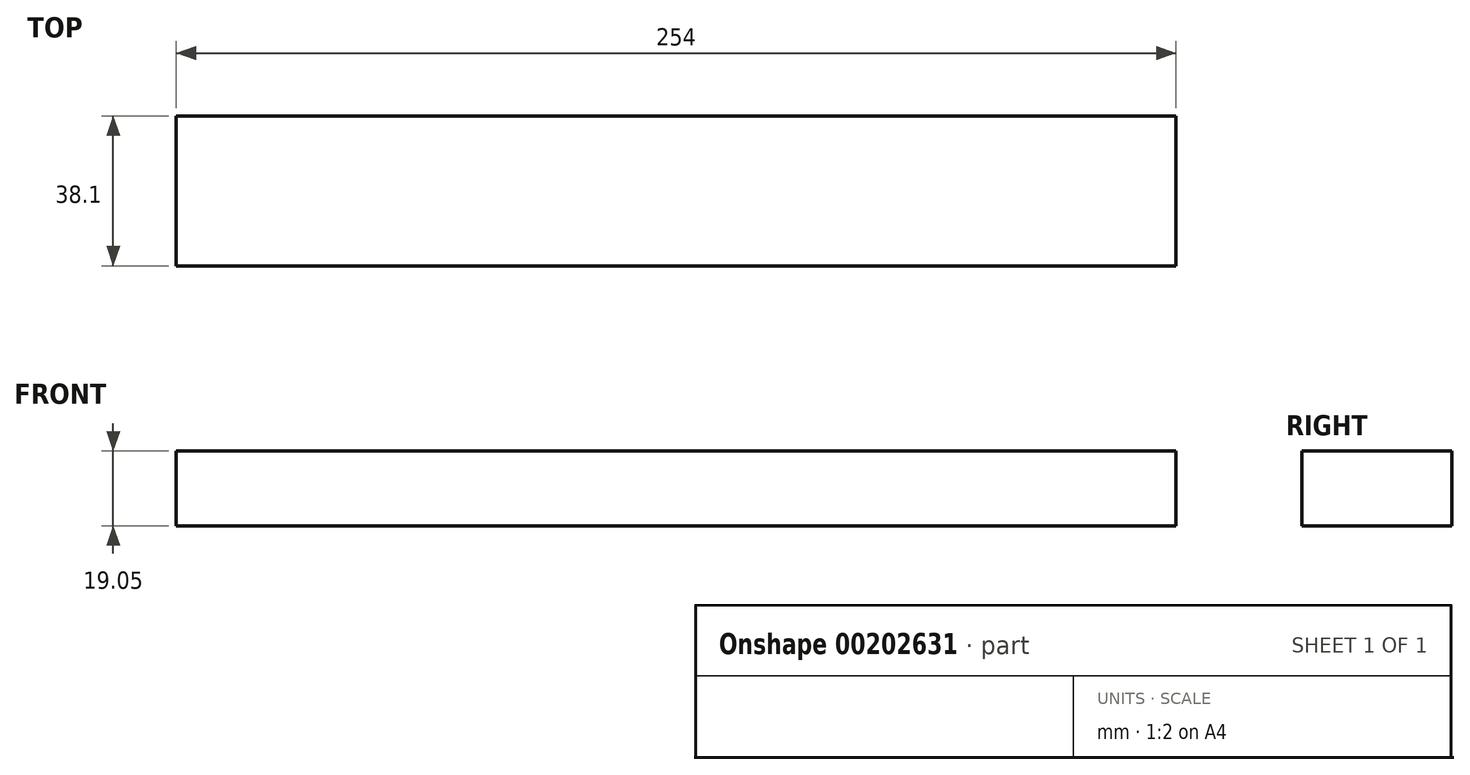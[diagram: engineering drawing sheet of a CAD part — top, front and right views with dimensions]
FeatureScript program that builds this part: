
annotation { "Feature Type Name" : "Feature", "Feature Type Description" : "" }
export const myFeature = defineFeature(function(context is Context, id is Id, definition is map)
    precondition{}
    {
        {
            var Q0;
            Q0=qCreatedBy(makeId("Top.planeOp"),FACE);
            var sketch = newSketch(context, id + "F0", { "sketchPlane" : qUnion([Q0])});
            skLineSegment(sketch, "E0.bottom", {"start": v(0, 0) * mm, "end": v(254, 0) * mm});
            skLineSegment(sketch, "E0.top", {"start": v(0, 38.1) * mm, "end": v(254, 38.1) * mm});
            skLineSegment(sketch, "E0.left", {"start": v(0, 0) * mm, "end": v(0, 38.1) * mm});
            skLineSegment(sketch, "E0.right", {"start": v(254, 0) * mm, "end": v(254, 38.1) * mm});
            skSolve(sketch);
        }
        {
            var Q0;
            Q0=makeQuery(id+"F0.imprint","IMPRINT",FACE,{"disambiguationData":[TD([[makeQuery(id+"F0.imprint","IMPRINT",EDGE,{"derivedFrom":sQuery(id+"F0.wireOp",EDGE,"E0.bottom")}),1.0]])]});
            extrude(context, id + "F1", {"entities" : qUnion([Q0]), "depth" : 19.05 * mm});
        }
    });
